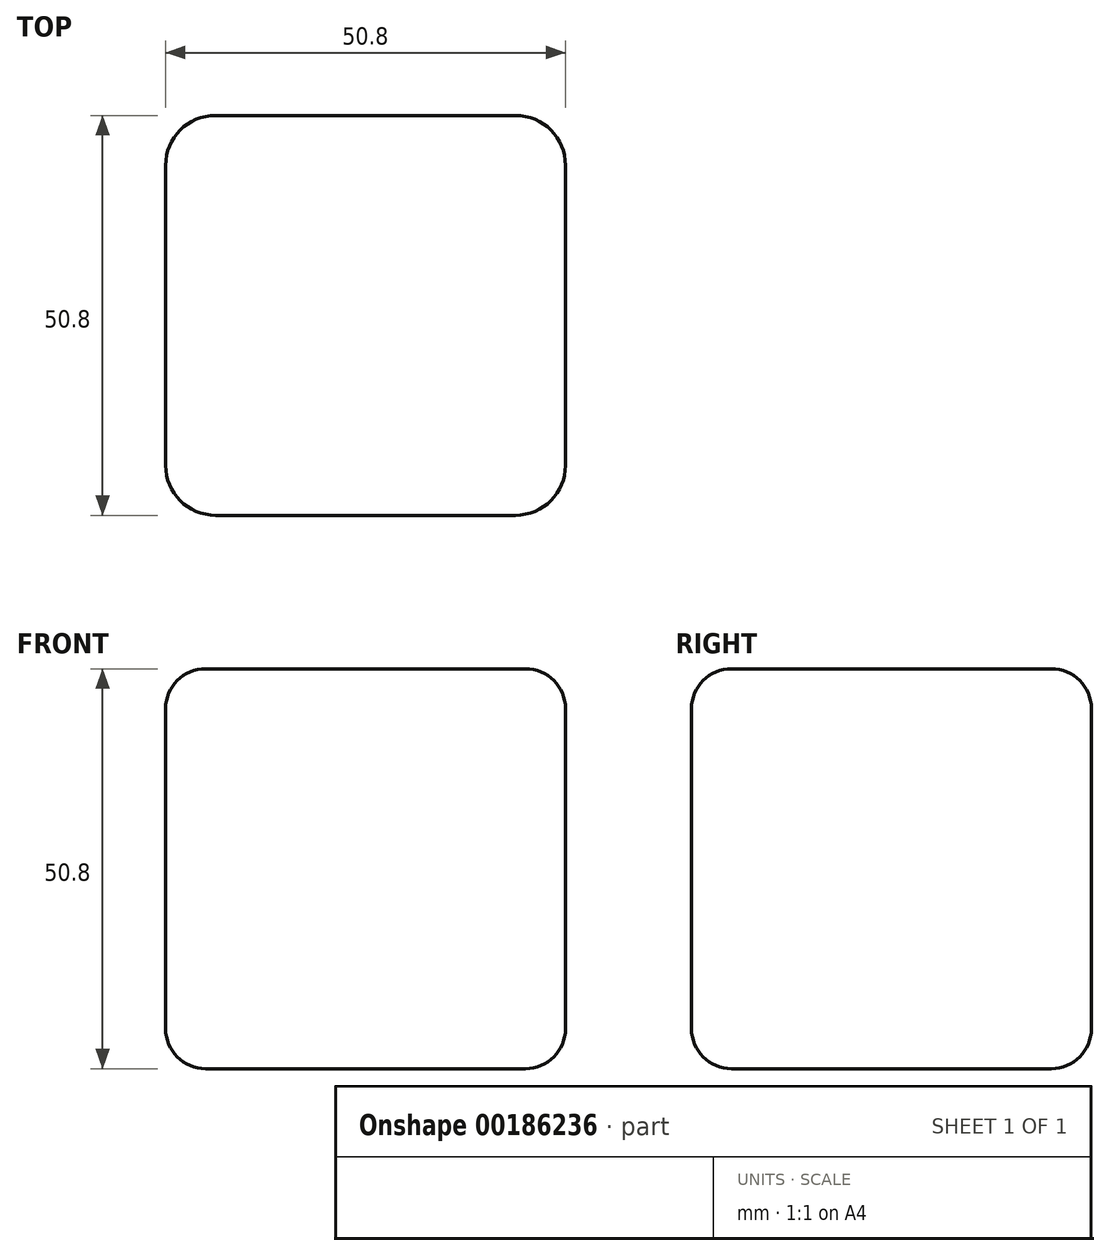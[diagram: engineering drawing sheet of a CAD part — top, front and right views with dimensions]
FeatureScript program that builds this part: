
annotation { "Feature Type Name" : "Feature", "Feature Type Description" : "" }
export const myFeature = defineFeature(function(context is Context, id is Id, definition is map)
    precondition{}
    {
        {
            var Q0;
            Q0=qCreatedBy(makeId("Top.planeOp"),FACE);
            var sketch = newSketch(context, id + "F0", { "sketchPlane" : qUnion([Q0])});
            skLineSegment(sketch, "E0.bottom", {"start": v(19.05, -25.4) * mm, "end": v(-19.05, -25.4) * mm});
            skLineSegment(sketch, "E0.top", {"start": v(19.05, 25.4) * mm, "end": v(-19.05, 25.4) * mm});
            skLineSegment(sketch, "E0.left", {"start": v(25.4, -19.05) * mm, "end": v(25.4, 19.05) * mm});
            skLineSegment(sketch, "E0.right", {"start": v(-25.4, -19.05) * mm, "end": v(-25.4, 19.05) * mm});
            skPoint(sketch, "E0.middle", {"position": v(0, 0) * mm});
            skPoint(sketch, "E1.visualSharp", {"position": v(25.4, 25.4) * mm});
            skArc(sketch, "E1.filletArc", {"start": v(25.4, 19.05) * mm, "mid": v(23.54, 23.54) * mm, "end": v(19.05, 25.4) * mm});
            skPoint(sketch, "E2.visualSharp", {"position": v(-25.4, 25.4) * mm});
            skArc(sketch, "E2.filletArc", {"start": v(-19.05, 25.4) * mm, "mid": v(-23.54, 23.54) * mm, "end": v(-25.4, 19.05) * mm});
            skPoint(sketch, "E3.visualSharp", {"position": v(-25.4, -25.4) * mm});
            skArc(sketch, "E3.filletArc", {"start": v(-25.4, -19.05) * mm, "mid": v(-23.54, -23.54) * mm, "end": v(-19.05, -25.4) * mm});
            skPoint(sketch, "E4.visualSharp", {"position": v(25.4, -25.4) * mm});
            skArc(sketch, "E4.filletArc", {"start": v(19.05, -25.4) * mm, "mid": v(23.54, -23.54) * mm, "end": v(25.4, -19.05) * mm});
            skSolve(sketch);
        }
        {
            var Q0;
            Q0 = qSketchRegion(id + "F0", true);
            extrude(context, id + "F1", {"entities" : qUnion([Q0]), "depth" : 50.8 * mm});
        }
        {
            var Q0;
            Q0=makeQuery(id+"F1.opExtrude","CAP_EDGE",EDGE,{"disambiguationData":[OSD([sQuery(id+"F0.wireOp",EDGE,"E0.right")])],"isStart":false});
            var Q1;
            Q1=makeQuery(id+"F1.opExtrude","CAP_EDGE",EDGE,{"disambiguationData":[OSD([sQuery(id+"F0.wireOp",EDGE,"E0.right")])],"isStart":true});
            fillet(context, id + "F2", {"entities" : qUnion([Q0, Q1]), "radius" : 5.08 * mm, "tangentPropagation" : true, "allowEdgeOverflow" : false});
        }
    });
